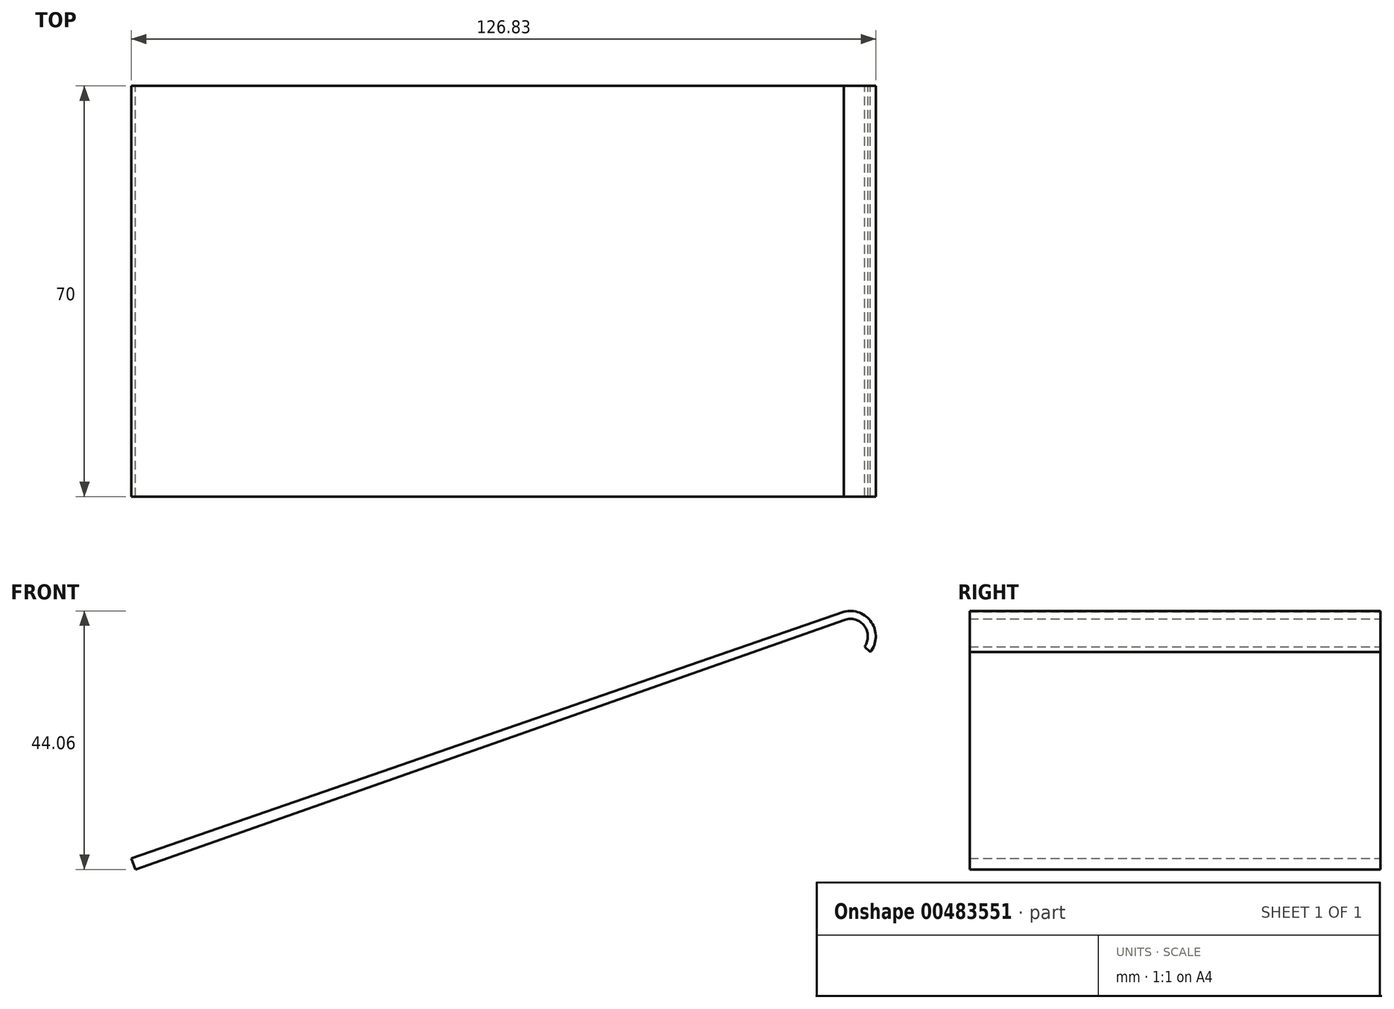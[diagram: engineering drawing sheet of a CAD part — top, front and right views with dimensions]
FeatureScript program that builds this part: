
annotation { "Feature Type Name" : "Feature", "Feature Type Description" : "" }
export const myFeature = defineFeature(function(context is Context, id is Id, definition is map)
    precondition{}
    {
        {
            var Q0;
            Q0=qCreatedBy(makeId("Front.planeOp"),FACE);
            var sketch = newSketch(context, id + "F0", { "sketchPlane" : qUnion([Q0])});
            skArc(sketch, "E0", {"start": v(42.12, 10.4) * mm, "mid": v(42.08, 13.95) * mm, "end": v(38.68, 14.98) * mm});
            skArc(sketch, "E1", {"start": v(43.11, 9.48) * mm, "mid": v(43.12, 14.82) * mm, "end": v(37.95, 16.14) * mm});
            skLineSegment(sketch, "E2", {"start": v(38.68, 14.98) * mm, "end": v(-82.14, -27.56) * mm});
            skLineSegment(sketch, "E3", {"start": v(-82.14, -27.56) * mm, "end": v(-82.8, -25.67) * mm});
            skLineSegment(sketch, "E4", {"start": v(-82.8, -25.67) * mm, "end": v(38.57, 16.36) * mm});
            skLineSegment(sketch, "E5", {"start": v(42.12, 10.4) * mm, "end": v(43.11, 9.48) * mm});
            skSolve(sketch);
        }
        {
            var Q0;
            Q0=makeQuery(id+"F0.imprint","IMPRINT",FACE,{"disambiguationData":[TD([[makeQuery(id+"F0.imprint","IMPRINT",EDGE,{"derivedFrom":sQuery(id+"F0.wireOp",EDGE,"E0")}),-1.0]])]});
            var Q1;
            Q1=sQuery(id+"F0.wireOp",EDGE,"E0");
            var Q2;
            Q2=sQuery(id+"F0.wireOp",EDGE,"E1");
            var Q3;
            Q3=sQuery(id+"F0.wireOp",EDGE,"E2");
            var Q4;
            Q4=sQuery(id+"F0.wireOp",EDGE,"E3");
            var Q5;
            Q5=sQuery(id+"F0.wireOp",EDGE,"E4");
            var Q6;
            Q6=sQuery(id+"F0.wireOp",EDGE,"E5");
            extrude(context, id + "F1", {"entities" : qUnion([Q0]), "surfaceEntities" : qUnion([Q1, Q2, Q3, Q4, Q5, Q6]), "depth" : 70 * mm});
        }
    });
